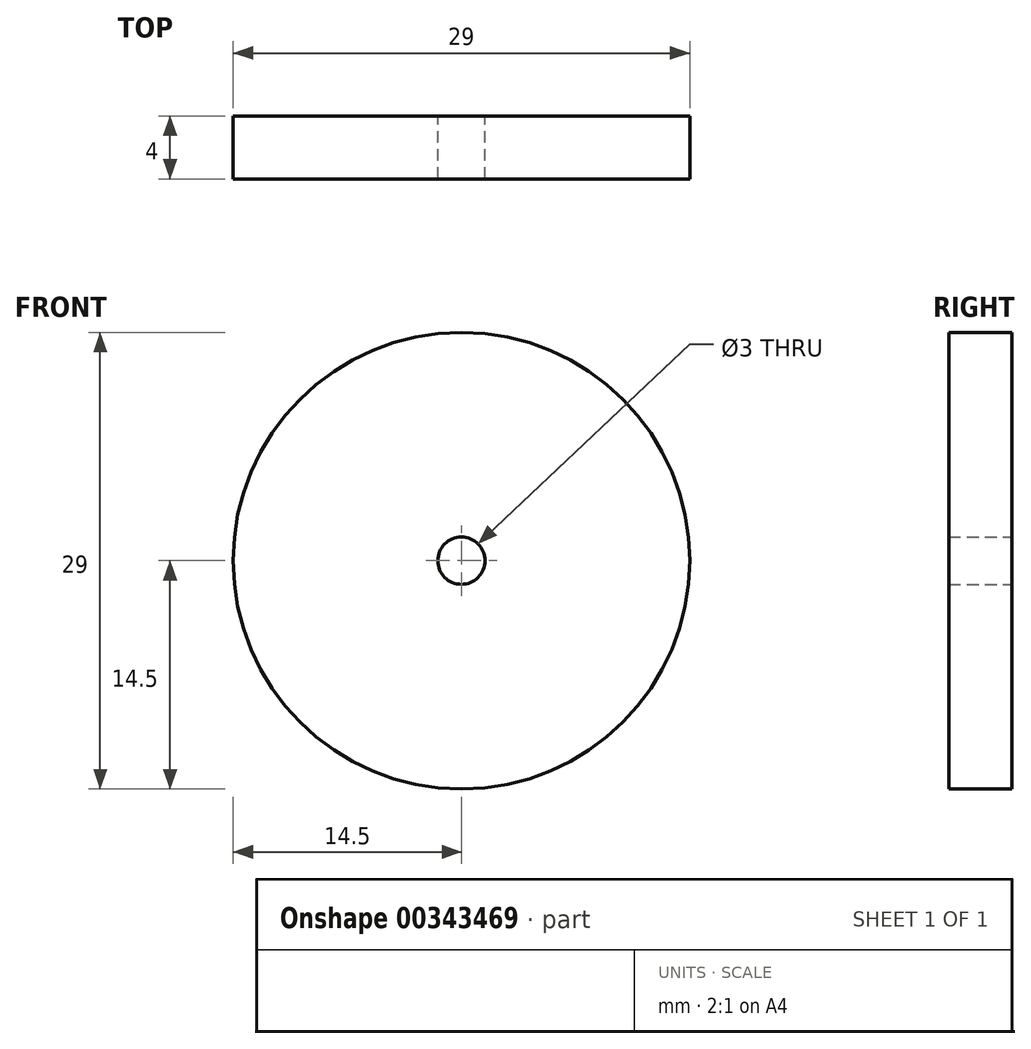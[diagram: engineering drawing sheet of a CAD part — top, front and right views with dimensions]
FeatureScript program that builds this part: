
annotation { "Feature Type Name" : "Feature", "Feature Type Description" : "" }
export const myFeature = defineFeature(function(context is Context, id is Id, definition is map)
    precondition{}
    {
        {
            var Q0;
            Q0=qCreatedBy(makeId("Front.planeOp"),FACE);
            var sketch = newSketch(context, id + "F0", { "sketchPlane" : qUnion([Q0])});
            skCircle(sketch, "E0", {"center": v(0, 0) * mm, "radius": 14.5 * mm});
            skCircle(sketch, "E1", {"center": v(0, 0) * mm, "radius": 1.5 * mm});
            skSolve(sketch);
        }
        {
            var Q0;
            Q0=makeQuery(id+"F0.imprint","IMPRINT",FACE,{"disambiguationData":[TD([[makeQuery(id+"F0.imprint","IMPRINT",EDGE,{"derivedFrom":sQuery(id+"F0.wireOp",EDGE,"E0")}),1.0]])]});
            extrude(context, id + "F1", {"entities" : qUnion([Q0]), "depth" : 4 * mm});
        }
    });
